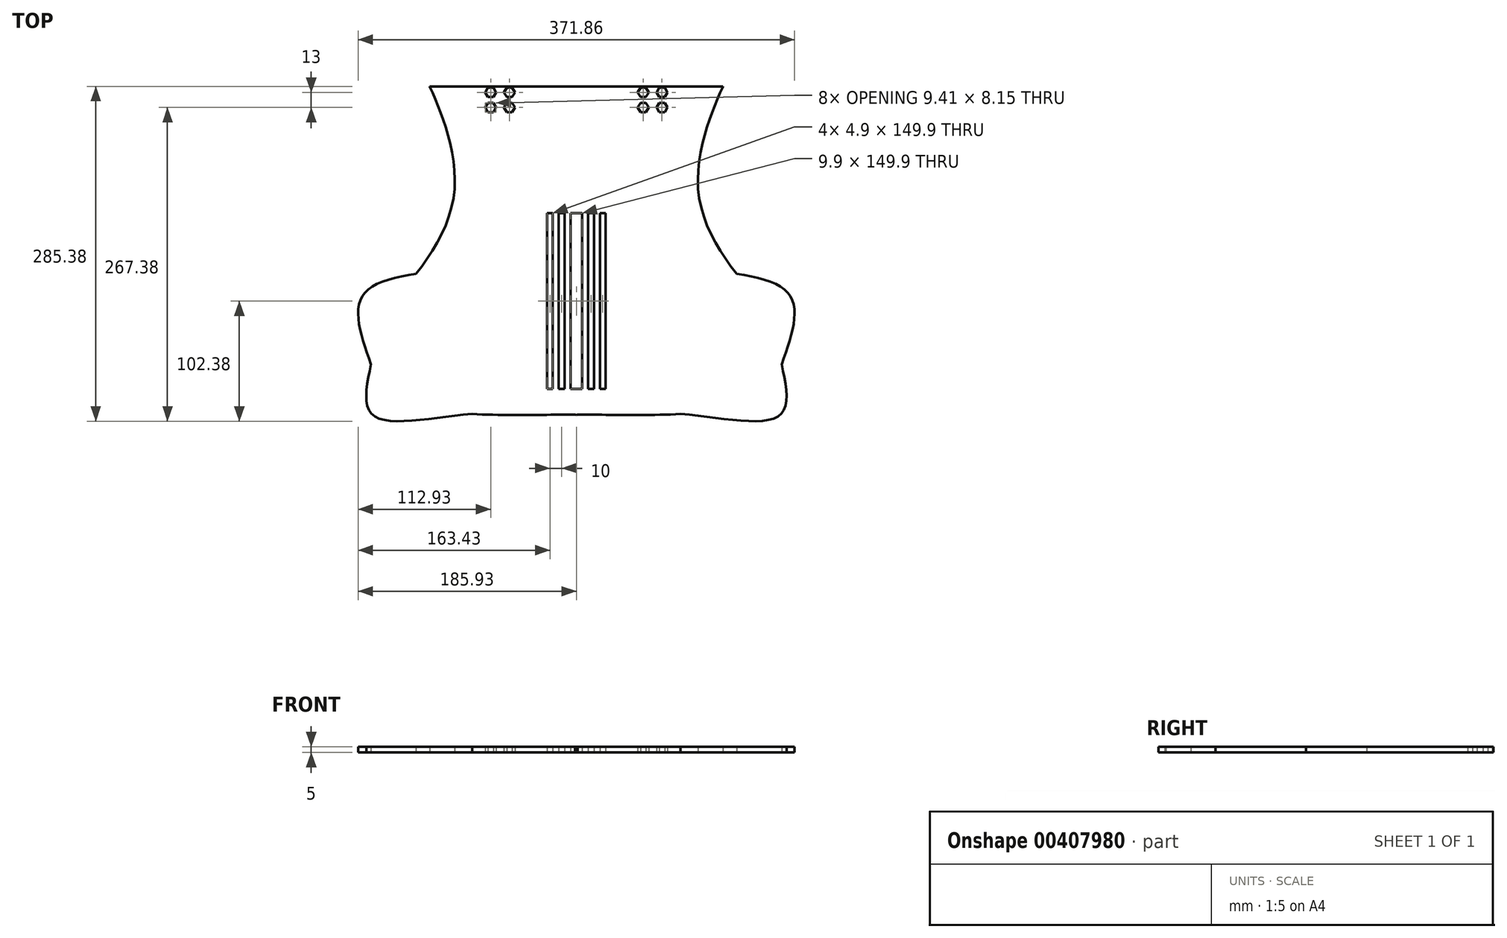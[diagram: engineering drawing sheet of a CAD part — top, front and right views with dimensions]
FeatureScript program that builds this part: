
annotation { "Feature Type Name" : "Feature", "Feature Type Description" : "" }
export const myFeature = defineFeature(function(context is Context, id is Id, definition is map)
    precondition{}
    {
        {
            var Q0;
            Q0=qCreatedBy(makeId("Top.planeOp"),FACE);
            var sketch = newSketch(context, id + "F0", { "sketchPlane" : qUnion([Q0])});
            skLineSegment(sketch, "E0.bottom", {"start": v(-125, 0) * mm, "end": v(125, 0) * mm, "construction": true});
            skLineSegment(sketch, "E0.top", {"start": v(-125, -280) * mm, "end": v(125, -280) * mm, "construction": true});
            skLineSegment(sketch, "E0.left", {"start": v(-125, 0) * mm, "end": v(-125, -280) * mm, "construction": true});
            skLineSegment(sketch, "E0.right", {"start": v(125, 0) * mm, "end": v(125, -280) * mm, "construction": true});
            skFitSpline(sketch, "E1", {"points": [v(-125, 0) * mm, v(-175, -236.88) * mm], "startDerivative": vector(163.58, -419.06) * mm, "endDerivative": vector(5.98, -192.46) * mm});
            skPoint(sketch, "E2", {"position": v(0, -280) * mm});
            skFitSpline(sketch, "E3", {"points": [v(-175, -236.88) * mm, v(0, -280) * mm], "startDerivative": vector(4.02, -129.37) * mm, "endDerivative": vector(290.73, 0) * mm});
            skFitSpline(sketch, "E4.MirrorCS", {"points": [v(125, 0) * mm, v(175, -236.88) * mm], "startDerivative": vector(-163.58, -419.06) * mm, "endDerivative": vector(-5.98, -192.46) * mm});
            skFitSpline(sketch, "E5.MirrorCS", {"points": [v(175, -236.88) * mm, v(0, -280) * mm], "startDerivative": vector(-4.02, -129.37) * mm, "endDerivative": vector(-290.73, 0) * mm});
            skFitSpline(sketch, "E6", {"points": [v(-125, 0) * mm, v(0, 25) * mm], "startDerivative": vector(-31, 79.42) * mm, "endDerivative": vector(148.36, 0.98) * mm});
            skFitSpline(sketch, "E7.MirrorCS", {"points": [v(125, 0) * mm, v(0, 25) * mm], "startDerivative": vector(31, 79.42) * mm, "endDerivative": vector(-148.36, 0.98) * mm});
            skLineSegment(sketch, "E8.bottom", {"start": v(-10, -88) * mm, "end": v(-5, -88) * mm, "construction": true});
            skLineSegment(sketch, "E8.top", {"start": v(-10, -278) * mm, "end": v(-5, -278) * mm, "construction": true});
            skLineSegment(sketch, "E8.left", {"start": v(-10, -88) * mm, "end": v(-10, -278) * mm, "construction": true});
            skLineSegment(sketch, "E8.right", {"start": v(-5, -88) * mm, "end": v(-5, -278) * mm, "construction": true});
            skLineSegment(sketch, "E9.1.0.0", {"start": v(-20, -88) * mm, "end": v(-20, -278) * mm, "construction": true});
            skLineSegment(sketch, "E9.1.0.1", {"start": v(-15, -88) * mm, "end": v(-15, -278) * mm, "construction": true});
            skLineSegment(sketch, "E9.1.0.2", {"start": v(-20, -88) * mm, "end": v(-15, -88) * mm, "construction": true});
            skLineSegment(sketch, "E9.1.0.3", {"start": v(-20, -278) * mm, "end": v(-15, -278) * mm, "construction": true});
            skLineSegment(sketch, "E9.2.0.0", {"start": v(-30, -88) * mm, "end": v(-30, -278) * mm, "construction": true});
            skLineSegment(sketch, "E9.2.0.1", {"start": v(-25, -88) * mm, "end": v(-25, -278) * mm, "construction": true});
            skLineSegment(sketch, "E9.2.0.2", {"start": v(-30, -88) * mm, "end": v(-25, -88) * mm, "construction": true});
            skLineSegment(sketch, "E9.2.0.3", {"start": v(-30, -278) * mm, "end": v(-25, -278) * mm, "construction": true});
            skLineSegment(sketch, "E9.direction1", {"start": v(-10, -278) * mm, "end": v(-20, -278) * mm, "construction": true});
            skLineSegment(sketch, "E10.MirrorCS", {"start": v(10, -278) * mm, "end": v(20, -278) * mm, "construction": true});
            skLineSegment(sketch, "E11.MirrorCS", {"start": v(20, -278) * mm, "end": v(15, -278) * mm, "construction": true});
            skLineSegment(sketch, "E12.MirrorCS", {"start": v(10, -278) * mm, "end": v(5, -278) * mm, "construction": true});
            skLineSegment(sketch, "E13.MirrorCS", {"start": v(20, -88) * mm, "end": v(15, -88) * mm, "construction": true});
            skLineSegment(sketch, "E14.MirrorCS", {"start": v(30, -278) * mm, "end": v(25, -278) * mm, "construction": true});
            skLineSegment(sketch, "E15.MirrorCS", {"start": v(10, -88) * mm, "end": v(5, -88) * mm, "construction": true});
            skLineSegment(sketch, "E16.MirrorCS", {"start": v(30, -88) * mm, "end": v(25, -88) * mm, "construction": true});
            skLineSegment(sketch, "E17.MirrorCS", {"start": v(30, -88) * mm, "end": v(30, -278) * mm, "construction": true});
            skLineSegment(sketch, "E18.MirrorCS", {"start": v(10, -88) * mm, "end": v(10, -278) * mm, "construction": true});
            skLineSegment(sketch, "E19.MirrorCS", {"start": v(15, -88) * mm, "end": v(15, -278) * mm, "construction": true});
            skLineSegment(sketch, "E20.MirrorCS", {"start": v(5, -88) * mm, "end": v(5, -278) * mm, "construction": true});
            skLineSegment(sketch, "E21.MirrorCS", {"start": v(20, -88) * mm, "end": v(20, -278) * mm, "construction": true});
            skLineSegment(sketch, "E22.MirrorCS", {"start": v(25, -88) * mm, "end": v(25, -278) * mm, "construction": true});
            skLineSegment(sketch, "E23.bottom", {"start": v(-73, -5) * mm, "end": v(-57, -5) * mm, "construction": true});
            skLineSegment(sketch, "E23.top", {"start": v(-73, -18) * mm, "end": v(-57, -18) * mm, "construction": true});
            skLineSegment(sketch, "E23.left", {"start": v(-73, -5) * mm, "end": v(-73, -18) * mm, "construction": true});
            skLineSegment(sketch, "E23.right", {"start": v(-57, -5) * mm, "end": v(-57, -18) * mm, "construction": true});
            skCircle(sketch, "E24", {"center": v(-73, -5) * mm, "radius": 2.02 * mm, "construction": true});
            skCircle(sketch, "E25", {"center": v(-57, -5) * mm, "radius": 2.02 * mm, "construction": true});
            skCircle(sketch, "E26", {"center": v(-57, -18) * mm, "radius": 2.02 * mm, "construction": true});
            skCircle(sketch, "E27", {"center": v(-73, -18) * mm, "radius": 2.02 * mm, "construction": true});
            skPoint(sketch, "E28", {"position": v(-65, -5) * mm});
            skLineSegment(sketch, "E29.MirrorCS", {"start": v(73, -18) * mm, "end": v(57, -18) * mm, "construction": true});
            skCircle(sketch, "E30.MirrorC", {"center": v(57, -5) * mm, "radius": 2.02 * mm, "construction": true});
            skCircle(sketch, "E31.MirrorC", {"center": v(57, -18) * mm, "radius": 2.02 * mm, "construction": true});
            skPoint(sketch, "E32.MirrorP", {"position": v(65, -5) * mm});
            skCircle(sketch, "E33.MirrorC", {"center": v(73, -5) * mm, "radius": 2.02 * mm, "construction": true});
            skLineSegment(sketch, "E34.MirrorCS", {"start": v(73, -5) * mm, "end": v(57, -5) * mm, "construction": true});
            skLineSegment(sketch, "E35.MirrorCS", {"start": v(57, -5) * mm, "end": v(57, -18) * mm, "construction": true});
            skCircle(sketch, "E36.MirrorC", {"center": v(73, -18) * mm, "radius": 2.02 * mm, "construction": true});
            skLineSegment(sketch, "E37.MirrorCS", {"start": v(73, -5) * mm, "end": v(73, -18) * mm, "construction": true});
            skSolve(sketch);
        }
        {
            var Q0;
            Q0=qCreatedBy(makeId("Top.planeOp"),FACE);
            var sketch = newSketch(context, id + "F1", { "sketchPlane" : qUnion([Q0])});
            skCircle(sketch, "E38.0", {"center": v(-73, -5) * mm, "radius": 2.02 * mm, "construction": true});
            skCircle(sketch, "E38.1", {"center": v(-57, -5) * mm, "radius": 2.02 * mm, "construction": true});
            skCircle(sketch, "E38.2", {"center": v(-57, -18) * mm, "radius": 2.02 * mm, "construction": true});
            skCircle(sketch, "E38.3", {"center": v(-73, -18) * mm, "radius": 2.02 * mm, "construction": true});
            skCircle(sketch, "E38.4", {"center": v(57, -18) * mm, "radius": 2.02 * mm, "construction": true});
            skCircle(sketch, "E38.5", {"center": v(57, -5) * mm, "radius": 2.02 * mm, "construction": true});
            skCircle(sketch, "E38.6", {"center": v(73, -18) * mm, "radius": 2.02 * mm, "construction": true});
            skCircle(sketch, "E38.7", {"center": v(73, -5) * mm, "radius": 2.02 * mm, "construction": true});
            skCircle(sketch, "E39.cCircle", {"center": v(-73, -5) * mm, "radius": 4.08 * mm, "construction": true});
            skLineSegment(sketch, "E39.0", {"start": v(-68.3, -5) * mm, "end": v(-70.65, -9.08) * mm});
            skLineSegment(sketch, "E39.1", {"start": v(-70.65, -9.07) * mm, "end": v(-75.35, -9.07) * mm});
            skLineSegment(sketch, "E39.2", {"start": v(-75.35, -9.08) * mm, "end": v(-77.7, -5) * mm});
            skLineSegment(sketch, "E39.3", {"start": v(-77.7, -5) * mm, "end": v(-75.35, -0.92) * mm});
            skLineSegment(sketch, "E39.4", {"start": v(-75.35, -0.92) * mm, "end": v(-70.65, -0.92) * mm});
            skLineSegment(sketch, "E39.5", {"start": v(-70.65, -0.93) * mm, "end": v(-68.3, -5) * mm});
            skPoint(sketch, "E39.0.midPoint", {"position": v(-69.47, -7.04) * mm});
            skCircle(sketch, "E40.cCircle", {"center": v(-57, -5) * mm, "radius": 4.08 * mm, "construction": true});
            skLineSegment(sketch, "E40.0", {"start": v(-52.3, -5) * mm, "end": v(-54.65, -9.08) * mm});
            skLineSegment(sketch, "E40.1", {"start": v(-54.65, -9.08) * mm, "end": v(-59.35, -9.08) * mm});
            skLineSegment(sketch, "E40.2", {"start": v(-59.35, -9.07) * mm, "end": v(-61.7, -5) * mm});
            skLineSegment(sketch, "E40.3", {"start": v(-61.7, -5) * mm, "end": v(-59.35, -0.92) * mm});
            skLineSegment(sketch, "E40.4", {"start": v(-59.35, -0.92) * mm, "end": v(-54.65, -0.92) * mm});
            skLineSegment(sketch, "E40.5", {"start": v(-54.65, -0.92) * mm, "end": v(-52.3, -5) * mm});
            skPoint(sketch, "E40.0.midPoint", {"position": v(-53.47, -7.04) * mm});
            skCircle(sketch, "E41.cCircle", {"center": v(-57, -18) * mm, "radius": 4.08 * mm, "construction": true});
            skLineSegment(sketch, "E41.0", {"start": v(-52.3, -18) * mm, "end": v(-54.65, -22.07) * mm});
            skLineSegment(sketch, "E41.1", {"start": v(-54.65, -22.07) * mm, "end": v(-59.35, -22.07) * mm});
            skLineSegment(sketch, "E41.2", {"start": v(-59.35, -22.08) * mm, "end": v(-61.7, -18) * mm});
            skLineSegment(sketch, "E41.3", {"start": v(-61.7, -18) * mm, "end": v(-59.35, -13.93) * mm});
            skLineSegment(sketch, "E41.4", {"start": v(-59.35, -13.93) * mm, "end": v(-54.65, -13.93) * mm});
            skLineSegment(sketch, "E41.5", {"start": v(-54.65, -13.93) * mm, "end": v(-52.3, -18) * mm});
            skPoint(sketch, "E41.0.midPoint", {"position": v(-53.47, -20.04) * mm});
            skCircle(sketch, "E42.cCircle", {"center": v(-73, -18) * mm, "radius": 4.08 * mm, "construction": true});
            skLineSegment(sketch, "E42.0", {"start": v(-68.3, -18) * mm, "end": v(-70.65, -22.07) * mm});
            skLineSegment(sketch, "E42.1", {"start": v(-70.65, -22.07) * mm, "end": v(-75.35, -22.07) * mm});
            skLineSegment(sketch, "E42.2", {"start": v(-75.35, -22.08) * mm, "end": v(-77.7, -18) * mm});
            skLineSegment(sketch, "E42.3", {"start": v(-77.7, -18) * mm, "end": v(-75.35, -13.93) * mm});
            skLineSegment(sketch, "E42.4", {"start": v(-75.35, -13.93) * mm, "end": v(-70.65, -13.93) * mm});
            skLineSegment(sketch, "E42.5", {"start": v(-70.65, -13.92) * mm, "end": v(-68.3, -18) * mm});
            skPoint(sketch, "E42.0.midPoint", {"position": v(-69.47, -20.04) * mm});
            skCircle(sketch, "E43.cCircle", {"center": v(57, -18) * mm, "radius": 4.07 * mm, "construction": true});
            skLineSegment(sketch, "E43.0", {"start": v(61.7, -18) * mm, "end": v(59.35, -22.08) * mm});
            skLineSegment(sketch, "E43.1", {"start": v(59.35, -22.07) * mm, "end": v(54.65, -22.07) * mm});
            skLineSegment(sketch, "E43.2", {"start": v(54.65, -22.07) * mm, "end": v(52.3, -18) * mm});
            skLineSegment(sketch, "E43.3", {"start": v(52.3, -18) * mm, "end": v(54.65, -13.92) * mm});
            skLineSegment(sketch, "E43.4", {"start": v(54.65, -13.92) * mm, "end": v(59.35, -13.92) * mm});
            skLineSegment(sketch, "E43.5", {"start": v(59.35, -13.93) * mm, "end": v(61.7, -18) * mm});
            skPoint(sketch, "E43.0.midPoint", {"position": v(60.53, -20.04) * mm});
            skCircle(sketch, "E44.cCircle", {"center": v(73, -18) * mm, "radius": 4.07 * mm, "construction": true});
            skLineSegment(sketch, "E44.0", {"start": v(77.7, -18) * mm, "end": v(75.35, -22.08) * mm});
            skLineSegment(sketch, "E44.1", {"start": v(75.35, -22.07) * mm, "end": v(70.65, -22.07) * mm});
            skLineSegment(sketch, "E44.2", {"start": v(70.65, -22.07) * mm, "end": v(68.3, -18) * mm});
            skLineSegment(sketch, "E44.3", {"start": v(68.3, -18) * mm, "end": v(70.65, -13.92) * mm});
            skLineSegment(sketch, "E44.4", {"start": v(70.65, -13.93) * mm, "end": v(75.35, -13.93) * mm});
            skLineSegment(sketch, "E44.5", {"start": v(75.35, -13.92) * mm, "end": v(77.7, -18) * mm});
            skPoint(sketch, "E44.0.midPoint", {"position": v(76.53, -20.04) * mm});
            skCircle(sketch, "E45.cCircle", {"center": v(73, -5) * mm, "radius": 4.08 * mm, "construction": true});
            skLineSegment(sketch, "E45.0", {"start": v(75.35, -0.93) * mm, "end": v(77.7, -5) * mm});
            skLineSegment(sketch, "E45.1", {"start": v(77.7, -5) * mm, "end": v(75.35, -9.08) * mm});
            skLineSegment(sketch, "E45.2", {"start": v(75.35, -9.07) * mm, "end": v(70.65, -9.07) * mm});
            skLineSegment(sketch, "E45.3", {"start": v(70.65, -9.08) * mm, "end": v(68.3, -5) * mm});
            skLineSegment(sketch, "E45.4", {"start": v(68.3, -5) * mm, "end": v(70.65, -0.92) * mm});
            skLineSegment(sketch, "E45.5", {"start": v(70.65, -0.92) * mm, "end": v(75.35, -0.92) * mm});
            skPoint(sketch, "E45.0.midPoint", {"position": v(76.53, -2.96) * mm});
            skCircle(sketch, "E46.cCircle", {"center": v(57, -5) * mm, "radius": 4.08 * mm, "construction": true});
            skLineSegment(sketch, "E46.0", {"start": v(61.7, -5) * mm, "end": v(59.35, -9.07) * mm});
            skLineSegment(sketch, "E46.1", {"start": v(59.35, -9.07) * mm, "end": v(54.65, -9.07) * mm});
            skLineSegment(sketch, "E46.2", {"start": v(54.65, -9.08) * mm, "end": v(52.3, -5) * mm});
            skLineSegment(sketch, "E46.3", {"start": v(52.3, -5) * mm, "end": v(54.65, -0.92) * mm});
            skLineSegment(sketch, "E46.4", {"start": v(54.65, -0.92) * mm, "end": v(59.35, -0.92) * mm});
            skLineSegment(sketch, "E46.5", {"start": v(59.35, -0.92) * mm, "end": v(61.7, -5) * mm});
            skPoint(sketch, "E46.0.midPoint", {"position": v(60.53, -7.04) * mm});
            skFitSpline(sketch, "E47.0", {"points": [v(-125, 0) * mm, v(-70.47, -139.69) * mm, v(-177, -172.72) * mm, v(-175, -236.88) * mm]});
            skFitSpline(sketch, "E47.1", {"points": [v(-175, -236.88) * mm, v(-173.66, -280) * mm, v(-96.91, -280) * mm, v(0, -280) * mm]});
            skFitSpline(sketch, "E47.2", {"points": [v(175, -236.88) * mm, v(173.66, -280) * mm, v(96.91, -280) * mm, v(0, -280) * mm]});
            skFitSpline(sketch, "E47.3", {"points": [v(125, 0) * mm, v(70.47, -139.69) * mm, v(177, -172.72) * mm, v(175, -236.88) * mm]});
            skLineSegment(sketch, "E47.4", {"start": v(-125, 0) * mm, "end": v(125, 0) * mm});
            skLineSegment(sketch, "E48.0", {"start": v(-25, -88) * mm, "end": v(-25, -278) * mm, "construction": true});
            skLineSegment(sketch, "E48.1", {"start": v(-30, -88) * mm, "end": v(-25, -88) * mm, "construction": true});
            skLineSegment(sketch, "E48.2", {"start": v(-30, -88) * mm, "end": v(-30, -278) * mm, "construction": true});
            skLineSegment(sketch, "E48.3", {"start": v(-20, -88) * mm, "end": v(-15, -88) * mm, "construction": true});
            skLineSegment(sketch, "E48.4", {"start": v(-20, -88) * mm, "end": v(-20, -278) * mm, "construction": true});
            skLineSegment(sketch, "E48.5", {"start": v(-15, -88) * mm, "end": v(-15, -278) * mm, "construction": true});
            skLineSegment(sketch, "E48.6", {"start": v(-10, -88) * mm, "end": v(-10, -278) * mm, "construction": true});
            skLineSegment(sketch, "E48.7", {"start": v(-10, -88) * mm, "end": v(-5, -88) * mm, "construction": true});
            skLineSegment(sketch, "E48.8", {"start": v(-5, -88) * mm, "end": v(-5, -278) * mm, "construction": true});
            skLineSegment(sketch, "E48.9", {"start": v(10, -88) * mm, "end": v(5, -88) * mm, "construction": true});
            skLineSegment(sketch, "E48.10", {"start": v(20, -88) * mm, "end": v(15, -88) * mm, "construction": true});
            skLineSegment(sketch, "E48.11", {"start": v(30, -88) * mm, "end": v(25, -88) * mm, "construction": true});
            skLineSegment(sketch, "E48.12", {"start": v(25, -88) * mm, "end": v(25, -278) * mm, "construction": true});
            skLineSegment(sketch, "E48.13", {"start": v(30, -88) * mm, "end": v(30, -278) * mm, "construction": true});
            skLineSegment(sketch, "E48.14", {"start": v(20, -88) * mm, "end": v(20, -278) * mm, "construction": true});
            skLineSegment(sketch, "E48.15", {"start": v(15, -88) * mm, "end": v(15, -278) * mm, "construction": true});
            skLineSegment(sketch, "E48.16", {"start": v(10, -88) * mm, "end": v(10, -278) * mm, "construction": true});
            skLineSegment(sketch, "E48.17", {"start": v(5, -88) * mm, "end": v(5, -278) * mm, "construction": true});
            skLineSegment(sketch, "E48.18", {"start": v(30, -278) * mm, "end": v(25, -278) * mm, "construction": true});
            skLineSegment(sketch, "E48.19", {"start": v(10, -278) * mm, "end": v(20, -278) * mm, "construction": true});
            skLineSegment(sketch, "E48.20", {"start": v(10, -278) * mm, "end": v(5, -278) * mm, "construction": true});
            skLineSegment(sketch, "E48.21", {"start": v(-10, -278) * mm, "end": v(-5, -278) * mm, "construction": true});
            skLineSegment(sketch, "E48.22", {"start": v(-10, -278) * mm, "end": v(-20, -278) * mm, "construction": true});
            skLineSegment(sketch, "E48.23", {"start": v(-30, -278) * mm, "end": v(-25, -278) * mm, "construction": true});
            skLineSegment(sketch, "E49.bottom", {"start": v(-25, -258) * mm, "end": v(-20, -258) * mm, "construction": true});
            skLineSegment(sketch, "E49.top", {"start": v(-25, -108) * mm, "end": v(-20, -108) * mm, "construction": true});
            skLineSegment(sketch, "E49.left", {"start": v(-25, -108) * mm, "end": v(-25, -258) * mm, "construction": true});
            skLineSegment(sketch, "E49.right", {"start": v(-20, -108) * mm, "end": v(-20, -258) * mm, "construction": true});
            skLineSegment(sketch, "E50.bottom", {"start": v(-15, -108) * mm, "end": v(-10, -108) * mm, "construction": true});
            skLineSegment(sketch, "E50.top", {"start": v(-15, -258) * mm, "end": v(-10, -258) * mm, "construction": true});
            skLineSegment(sketch, "E50.left", {"start": v(-15, -258) * mm, "end": v(-15, -108) * mm, "construction": true});
            skLineSegment(sketch, "E50.right", {"start": v(-10, -258) * mm, "end": v(-10, -108) * mm, "construction": true});
            skLineSegment(sketch, "E51.bottom", {"start": v(-5, -258) * mm, "end": v(5, -258) * mm, "construction": true});
            skLineSegment(sketch, "E51.top", {"start": v(-5, -108) * mm, "end": v(5, -108) * mm, "construction": true});
            skLineSegment(sketch, "E51.left", {"start": v(-5, -108) * mm, "end": v(-5, -258) * mm, "construction": true});
            skLineSegment(sketch, "E51.right", {"start": v(5, -108) * mm, "end": v(5, -258) * mm, "construction": true});
            skLineSegment(sketch, "E52.bottom", {"start": v(10, -258) * mm, "end": v(15, -258) * mm, "construction": true});
            skLineSegment(sketch, "E52.top", {"start": v(10, -108) * mm, "end": v(15, -108) * mm, "construction": true});
            skLineSegment(sketch, "E52.left", {"start": v(10, -108) * mm, "end": v(10, -258) * mm, "construction": true});
            skLineSegment(sketch, "E52.right", {"start": v(15, -108) * mm, "end": v(15, -258) * mm, "construction": true});
            skLineSegment(sketch, "E53.bottom", {"start": v(20, -108) * mm, "end": v(25, -108) * mm, "construction": true});
            skLineSegment(sketch, "E53.top", {"start": v(20, -258) * mm, "end": v(25, -258) * mm, "construction": true});
            skLineSegment(sketch, "E53.left", {"start": v(20, -258) * mm, "end": v(20, -108) * mm, "construction": true});
            skLineSegment(sketch, "E53.right", {"start": v(25, -258) * mm, "end": v(25, -108) * mm, "construction": true});
            skPoint(sketch, "E54", {"position": v(-25, -183) * mm});
            skPoint(sketch, "E55", {"position": v(-20, -183) * mm});
            skPoint(sketch, "E56", {"position": v(-15, -183) * mm});
            skPoint(sketch, "E57", {"position": v(-10, -183) * mm});
            skPoint(sketch, "E58", {"position": v(-5, -183) * mm});
            skPoint(sketch, "E59", {"position": v(5, -183) * mm});
            skPoint(sketch, "E60", {"position": v(15, -183) * mm});
            skPoint(sketch, "E61", {"position": v(10, -183) * mm});
            skPoint(sketch, "E62", {"position": v(20, -183) * mm});
            skPoint(sketch, "E63", {"position": v(25, -183) * mm});
            skLineSegment(sketch, "E64.0", {"start": v(-24.95, -108.05) * mm, "end": v(-20.05, -108.05) * mm});
            skLineSegment(sketch, "E64.1", {"start": v(-24.95, -108.05) * mm, "end": v(-24.95, -257.95) * mm});
            skLineSegment(sketch, "E64.2", {"start": v(-24.95, -257.95) * mm, "end": v(-20.05, -257.95) * mm});
            skLineSegment(sketch, "E64.3", {"start": v(-20.05, -108.05) * mm, "end": v(-20.05, -257.95) * mm});
            skFitSpline(sketch, "E65.0", {"points": [v(0, -279.95) * mm, v(24.23, -279.95) * mm, v(70.16, -279.95) * mm, v(116.96, -276.58) * mm, v(145.43, -269.85) * mm, v(161.65, -262.27) * mm, v(172.1, -251.67) * mm, v(174.78, -242.26) * mm, v(174.95, -236.88) * mm]});
            skFitSpline(sketch, "E65.1", {"points": [v(124.95, 0.02) * mm, v(125.6, 1.67) * mm, v(126.13, 4.74) * mm, v(124.9, 8.73) * mm, v(121.79, 12.16) * mm, v(115.41, 16.03) * mm, v(103.75, 19.67) * mm, v(85.38, 22.46) * mm, v(64.21, 24.02) * mm, v(34.32, 24.95) * mm, v(12.36, 24.87) * mm, v(0, 24.95) * mm], "construction": true});
            skFitSpline(sketch, "E65.2", {"points": [v(0, 24.95) * mm, v(-12.36, 24.87) * mm, v(-34.32, 24.95) * mm, v(-64.21, 24.02) * mm, v(-85.38, 22.46) * mm, v(-103.75, 19.67) * mm, v(-115.41, 16.03) * mm, v(-121.79, 12.16) * mm, v(-124.9, 8.73) * mm, v(-126.13, 4.74) * mm, v(-125.6, 1.67) * mm, v(-124.95, 0.02) * mm], "construction": true});
            skFitSpline(sketch, "E65.3", {"points": [v(174.95, -236.88) * mm, v(175.45, -220.85) * mm, v(162.9, -192.68) * mm, v(128.62, -149.15) * mm, v(104.18, -91.44) * mm, v(111.32, -34.9) * mm, v(124.95, 0.02) * mm]});
            skFitSpline(sketch, "E65.4", {"points": [v(-124.95, 0.02) * mm, v(-111.32, -34.9) * mm, v(-104.18, -91.44) * mm, v(-128.62, -149.15) * mm, v(-162.9, -192.68) * mm, v(-175.45, -220.85) * mm, v(-174.95, -236.88) * mm]});
            skFitSpline(sketch, "E65.5", {"points": [v(-174.95, -236.88) * mm, v(-174.78, -242.26) * mm, v(-172.1, -251.67) * mm, v(-161.65, -262.27) * mm, v(-145.43, -269.85) * mm, v(-116.96, -276.58) * mm, v(-70.16, -279.95) * mm, v(-24.23, -279.95) * mm, v(0, -279.95) * mm]});
            skLineSegment(sketch, "E66.0", {"start": v(-14.95, -108.05) * mm, "end": v(-10.05, -108.05) * mm});
            skLineSegment(sketch, "E66.1", {"start": v(-14.95, -257.95) * mm, "end": v(-14.95, -108.05) * mm});
            skLineSegment(sketch, "E66.2", {"start": v(-14.95, -257.95) * mm, "end": v(-10.05, -257.95) * mm});
            skLineSegment(sketch, "E66.3", {"start": v(-10.05, -257.95) * mm, "end": v(-10.05, -108.05) * mm});
            skLineSegment(sketch, "E67.0", {"start": v(-4.95, -108.05) * mm, "end": v(-4.95, -257.95) * mm});
            skLineSegment(sketch, "E67.1", {"start": v(-4.95, -108.05) * mm, "end": v(4.95, -108.05) * mm});
            skLineSegment(sketch, "E67.2", {"start": v(4.95, -108.05) * mm, "end": v(4.95, -257.95) * mm});
            skLineSegment(sketch, "E67.3", {"start": v(-4.95, -257.95) * mm, "end": v(4.95, -257.95) * mm});
            skLineSegment(sketch, "E68.0", {"start": v(10.05, -108.05) * mm, "end": v(14.95, -108.05) * mm});
            skLineSegment(sketch, "E68.1", {"start": v(10.05, -108.05) * mm, "end": v(10.05, -257.95) * mm});
            skLineSegment(sketch, "E68.2", {"start": v(10.05, -257.95) * mm, "end": v(14.95, -257.95) * mm});
            skLineSegment(sketch, "E68.3", {"start": v(14.95, -108.05) * mm, "end": v(14.95, -257.95) * mm});
            skLineSegment(sketch, "E69.0", {"start": v(20.05, -257.95) * mm, "end": v(24.95, -257.95) * mm});
            skLineSegment(sketch, "E69.1", {"start": v(20.05, -257.95) * mm, "end": v(20.05, -108.05) * mm});
            skLineSegment(sketch, "E69.2", {"start": v(20.05, -108.05) * mm, "end": v(24.95, -108.05) * mm});
            skLineSegment(sketch, "E69.3", {"start": v(24.95, -257.95) * mm, "end": v(24.95, -108.05) * mm});
            skSolve(sketch);
        }
        {
            var Q0;
            Q0 = qSketchRegion(id + "F1", true);
            extrude(context, id + "F2", {"entities" : qUnion([Q0]), "depth" : 5 * mm});
        }
    });
